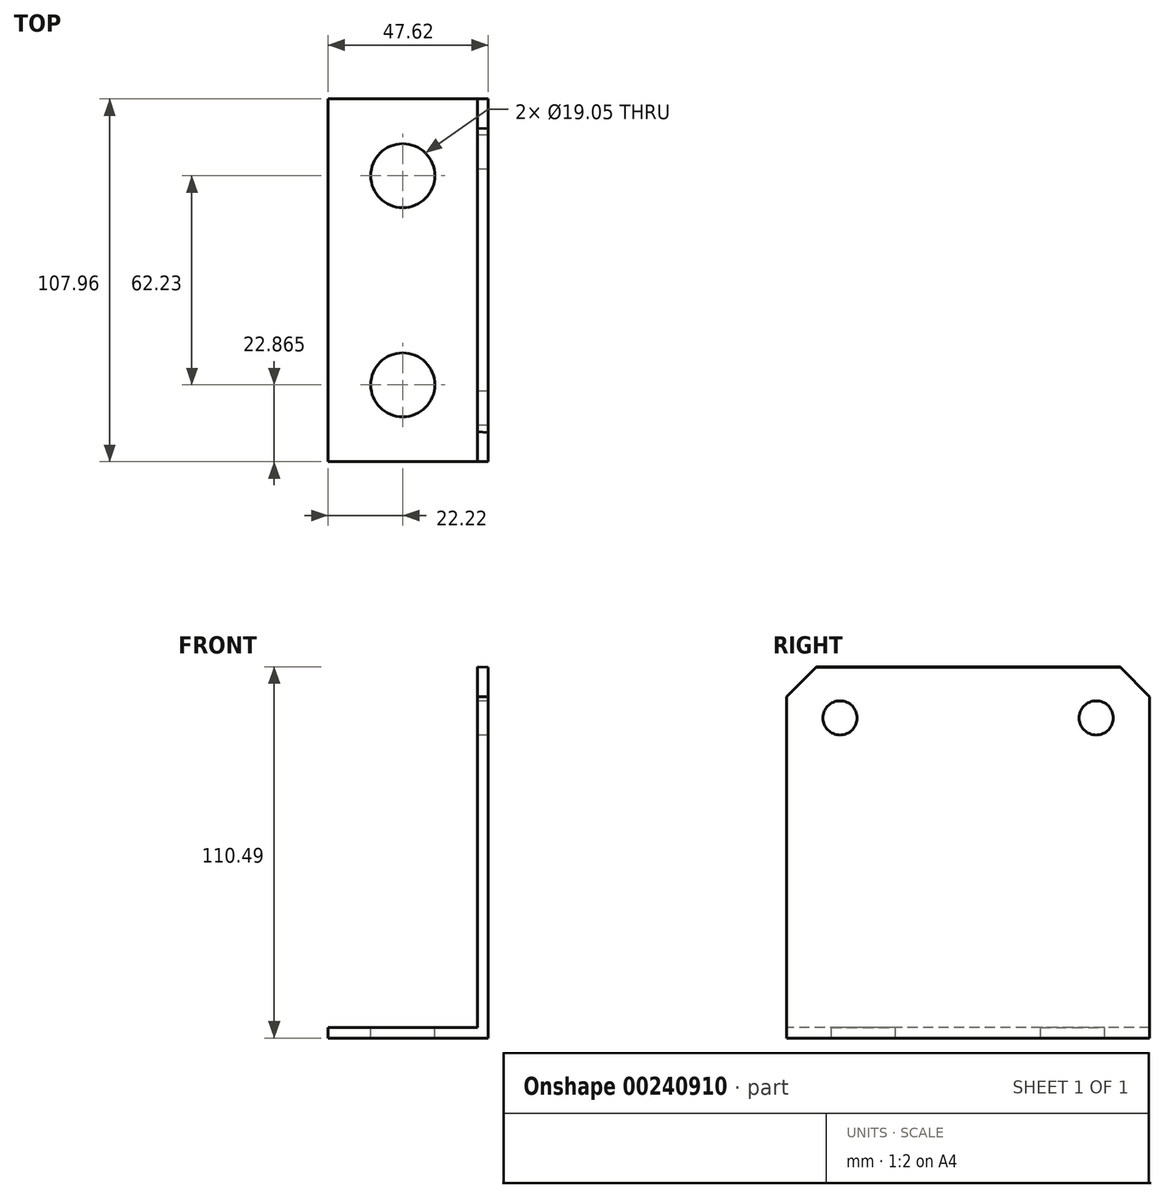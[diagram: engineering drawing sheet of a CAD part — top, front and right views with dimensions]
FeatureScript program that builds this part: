
annotation { "Feature Type Name" : "Feature", "Feature Type Description" : "" }
export const myFeature = defineFeature(function(context is Context, id is Id, definition is map)
    precondition{}
    {
        {
            var Q0;
            Q0=qCreatedBy(makeId("Right.planeOp"),FACE);
            var sketch = newSketch(context, id + "F0", { "sketchPlane" : qUnion([Q0])});
            skLineSegment(sketch, "E0.bottom", {"start": v(28.57, 63.5) * mm, "end": v(-28.57, 63.5) * mm});
            skLineSegment(sketch, "E0.top", {"start": v(53.97, -63.5) * mm, "end": v(-53.97, -63.5) * mm});
            skLineSegment(sketch, "E0.left", {"start": v(53.98, 38.1) * mm, "end": v(53.98, -63.5) * mm});
            skLineSegment(sketch, "E0.right", {"start": v(-53.98, 38.1) * mm, "end": v(-53.97, -63.5) * mm});
            skPoint(sketch, "E0.middle", {"position": v(0, 0) * mm});
            skLineSegment(sketch, "E1", {"start": v(0, 0) * mm, "end": v(0, 94.6) * mm, "construction": true});
            skPoint(sketch, "E1.endSnap0", {"position": v(0, 63.5) * mm});
            skLineSegment(sketch, "E2", {"start": v(-53.98, 38.1) * mm, "end": v(-28.57, 63.5) * mm});
            skLineSegment(sketch, "E3.MirrorCS", {"start": v(53.97, 38.1) * mm, "end": v(28.57, 63.5) * mm});
            skPoint(sketch, "E4.orphan", {"position": v(-53.98, 63.5) * mm});
            skPoint(sketch, "E5.orphan", {"position": v(53.98, 63.5) * mm});
            skSolve(sketch);
        }
        {
            var Q0;
            Q0=qSketchRegion(id+"F0",true);
            extrude(context, id + "F1", {"entities" : qUnion([Q0]), "depth" : 3.17 * mm});
        }
        {
            var Q0;
            Q0=makeQuery(id+"F1.opExtrude","SWEPT_FACE",FACE,{"disambiguationData":[OSD([sQuery(id+"F0.wireOp",EDGE,"E0.right")])]});
            var sketch = newSketch(context, id + "F2", { "sketchPlane" : qUnion([Q0])});
            skLineSegment(sketch, "E6", {"start": v(3.18, -63.5) * mm, "end": v(47.62, -63.5) * mm});
            skLineSegment(sketch, "E7", {"start": v(47.62, -63.5) * mm, "end": v(47.62, -60.33) * mm});
            skLineSegment(sketch, "E8", {"start": v(47.62, -60.33) * mm, "end": v(3.17, -60.33) * mm});
            skLineSegment(sketch, "E9", {"start": v(3.17, -60.33) * mm, "end": v(3.18, -63.5) * mm});
            skSolve(sketch);
        }
        {
            var Q0;
            Q0=qSketchRegion(id+"F2",true);
            var Q1;
            Q1=makeQuery(id+"F1.opExtrude","SWEPT_FACE",FACE,{"disambiguationData":[OSD([sQuery(id+"F0.wireOp",EDGE,"E0.left")])]});
            extrude(context, id + "F3", {"entities" : qUnion([Q0]), "operationType" : NewBodyOperationType.ADD, "endBound" : BoundingType.UP_TO_SURFACE, "oppositeDirection" : true, "endBoundEntityFace" : qUnion([Q1]), "depth" : 25.4 * mm});
        }
        {
            var Q0;
            Q0=makeQuery(id+"F1.opExtrude","CAP_FACE",FACE,{"disambiguationData":[OSD([sQuery(id+"F0.wireOp",EDGE,"E0.bottom"),sQuery(id+"F0.wireOp",EDGE,"E0.top"),sQuery(id+"F0.wireOp",EDGE,"E0.left"),sQuery(id+"F0.wireOp",EDGE,"E0.right")])],"isStart":false});
            var sketch = newSketch(context, id + "F4", { "sketchPlane" : qUnion([Q0])});
            skCircle(sketch, "E10", {"center": v(-38.1, 31.75) * mm, "radius": 5.08 * mm});
            skCircle(sketch, "E11", {"center": v(38.1, 31.75) * mm, "radius": 5.08 * mm});
            skSolve(sketch);
        }
        {
            var Q0;
            Q0=qSketchRegion(id+"F4",true);
            var Q1;
            Q1=makeQuery(id+"F1.opExtrude","CAP_FACE",FACE,{"disambiguationData":[OSD([sQuery(id+"F0.wireOp",EDGE,"E0.bottom"),sQuery(id+"F0.wireOp",EDGE,"E0.top"),sQuery(id+"F0.wireOp",EDGE,"E0.left"),sQuery(id+"F0.wireOp",EDGE,"E0.right"),sQuery(id+"F0.wireOp",EDGE,"E2"),sQuery(id+"F0.wireOp",EDGE,"E3.MirrorCS")])],"isStart":true});
            extrude(context, id + "F5", {"entities" : qUnion([Q0]), "operationType" : NewBodyOperationType.REMOVE, "endBound" : BoundingType.UP_TO_SURFACE, "oppositeDirection" : true, "endBoundEntityFace" : qUnion([Q1]), "depth" : 25.4 * mm});
        }
        {
            var Q0;
            Q0=makeQuery(id+"F3.opExtrude","SWEPT_FACE",FACE,{"disambiguationData":[OSD([sQuery(id+"F2.wireOp",EDGE,"E8")])]});
            var sketch = newSketch(context, id + "F6", { "sketchPlane" : qUnion([Q0])});
            skLineSegment(sketch, "E12", {"start": v(0, 0) * mm, "end": v(0, 50.21) * mm, "construction": true});
            skPoint(sketch, "E13.centerSnap0", {"position": v(25.4, -53.97) * mm});
            skLineSegment(sketch, "E14", {"start": v(0, 0) * mm, "end": v(-46.47, 0) * mm, "construction": true});
            skCircle(sketch, "E15", {"center": v(25.4, 31.11) * mm, "radius": 9.53 * mm});
            skPoint(sketch, "E15.centerSnap0", {"position": v(25.4, 53.97) * mm});
            skCircle(sketch, "E16.MirrorC", {"center": v(25.4, -31.11) * mm, "radius": 9.53 * mm});
            skSolve(sketch);
        }
        {
            var Q0;
            Q0=qSketchRegion(id+"F6",true);
            var Q1;
            Q1=makeQuery(id+"F3.boolean.opBoolean","MERGE",FACE,{"derivedFrom":[makeQuery(id+"F1.opExtrude","SWEPT_FACE",FACE,{"disambiguationData":[OSD([sQuery(id+"F0.wireOp",EDGE,"E0.top")])]}),makeQuery(id+"F3.opExtrude","SWEPT_FACE",FACE,{"disambiguationData":[OSD([sQuery(id+"F2.wireOp",EDGE,"E6")])]})]});
            extrude(context, id + "F7", {"entities" : qUnion([Q0]), "operationType" : NewBodyOperationType.REMOVE, "endBound" : BoundingType.UP_TO_SURFACE, "oppositeDirection" : true, "endBoundEntityFace" : qUnion([Q1]), "depth" : 25.4 * mm});
        }
        {
            var Q0;
            Q0=qSketchRegion(id+"F6",true);
            var Q1;
            Q1=makeQuery(id+"F3.boolean.opBoolean","MERGE",FACE,{"derivedFrom":[makeQuery(id+"F1.opExtrude","SWEPT_FACE",FACE,{"disambiguationData":[OSD([sQuery(id+"F0.wireOp",EDGE,"E0.top")])]}),makeQuery(id+"F3.opExtrude","SWEPT_FACE",FACE,{"disambiguationData":[OSD([sQuery(id+"F2.wireOp",EDGE,"E6")])]})]});
            extrude(context, id + "F8", {"entities" : qUnion([Q0]), "operationType" : NewBodyOperationType.REMOVE, "endBound" : BoundingType.UP_TO_SURFACE, "oppositeDirection" : true, "endBoundEntityFace" : qUnion([Q1]), "depth" : 25.4 * mm});
        }
        {
            var Q0;
            Q0=makeQuery(id+"F1.opExtrude","SWEPT_BODY",BODY,{"disambiguationData":[OSD([sQuery(id+"F0.wireOp",EDGE,"E0.bottom"),sQuery(id+"F0.wireOp",EDGE,"E0.top"),sQuery(id+"F0.wireOp",EDGE,"E0.left"),sQuery(id+"F0.wireOp",EDGE,"E0.right"),sQuery(id+"F0.wireOp",EDGE,"E2"),sQuery(id+"F0.wireOp",EDGE,"E3.MirrorCS")])]});
            var Q1;
            Q1=qCreatedBy(makeId("Right.planeOp"),FACE);
            mirror(context, id + "F9", {"entities" : qUnion([Q0]), "mirrorPlane" : qUnion([Q1])});
        }
        {
            var Q0;
            Q0=makeQuery(id+"F1.opExtrude","SWEPT_BODY",BODY,{"disambiguationData":[OSD([sQuery(id+"F0.wireOp",EDGE,"E0.bottom"),sQuery(id+"F0.wireOp",EDGE,"E0.top"),sQuery(id+"F0.wireOp",EDGE,"E0.left"),sQuery(id+"F0.wireOp",EDGE,"E0.right"),sQuery(id+"F0.wireOp",EDGE,"E2"),sQuery(id+"F0.wireOp",EDGE,"E3.MirrorCS")])]});
            deleteBodies(context, id + "F10", {"entities" : qUnion([Q0])});
        }
        {
            var Q0;
            Q0=makeQuery(id+"F9.opPattern","COPY",FACE,{"derivedFrom":makeQuery(id+"F1.opExtrude","CAP_FACE",FACE,{"disambiguationData":[OSD([sQuery(id+"F0.wireOp",EDGE,"E0.bottom"),sQuery(id+"F0.wireOp",EDGE,"E0.top"),sQuery(id+"F0.wireOp",EDGE,"E0.left"),sQuery(id+"F0.wireOp",EDGE,"E0.right"),sQuery(id+"F0.wireOp",EDGE,"E2"),sQuery(id+"F0.wireOp",EDGE,"E3.MirrorCS")])],"isStart":false}),"instanceName":"1"});
            var sketch = newSketch(context, id + "F11", { "sketchPlane" : qUnion([Q0])});
            skLineSegment(sketch, "E17", {"start": v(-28.57, 63.5) * mm, "end": v(28.57, 63.5) * mm});
            skLineSegment(sketch, "E18", {"start": v(28.57, 63.5) * mm, "end": v(45.09, 46.99) * mm});
            skLineSegment(sketch, "E19", {"start": v(45.09, 46.99) * mm, "end": v(-45.09, 46.99) * mm});
            skLineSegment(sketch, "E20", {"start": v(-45.09, 46.99) * mm, "end": v(-28.58, 63.5) * mm});
            skSolve(sketch);
        }
        {
            var Q0;
            Q0=qSketchRegion(id+"F11",true);
            var Q1;
            Q1=makeQuery(id+"F9.opPattern","COPY",FACE,{"derivedFrom":makeQuery(id+"F1.opExtrude","CAP_FACE",FACE,{"disambiguationData":[OSD([sQuery(id+"F0.wireOp",EDGE,"E0.bottom"),sQuery(id+"F0.wireOp",EDGE,"E0.top"),sQuery(id+"F0.wireOp",EDGE,"E0.left"),sQuery(id+"F0.wireOp",EDGE,"E0.right"),sQuery(id+"F0.wireOp",EDGE,"E2"),sQuery(id+"F0.wireOp",EDGE,"E3.MirrorCS")])],"isStart":true}),"instanceName":"1"});
            extrude(context, id + "F12", {"entities" : qUnion([Q0]), "operationType" : NewBodyOperationType.REMOVE, "endBound" : BoundingType.UP_TO_SURFACE, "oppositeDirection" : true, "endBoundEntityFace" : qUnion([Q1]), "depth" : 25.4 * mm, "hasDraft" : true, "draftAngle" : 3 * degree});
        }
    });
